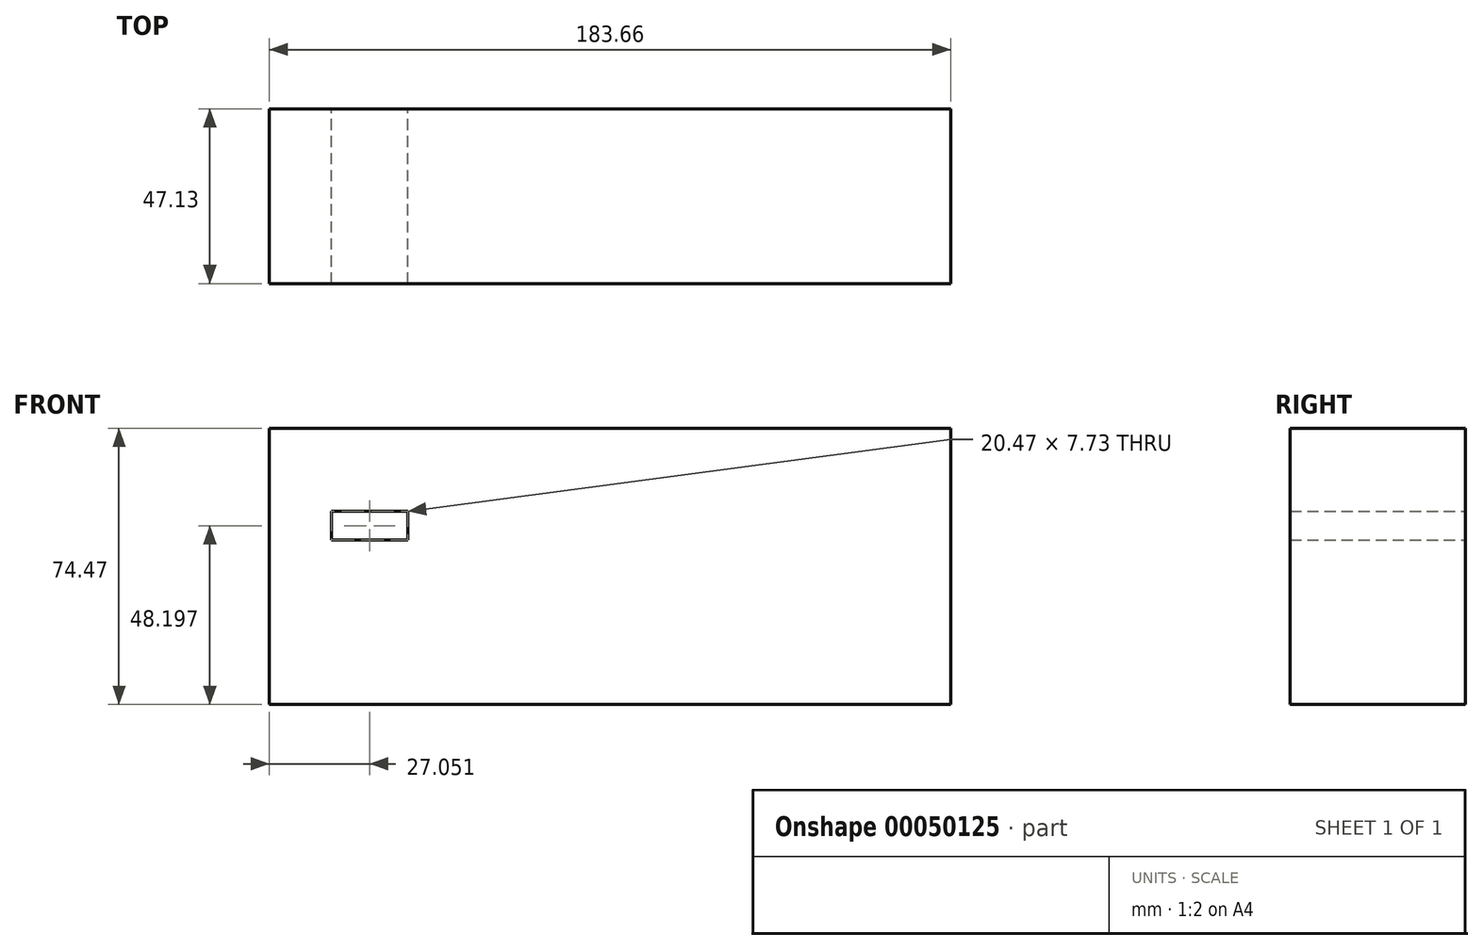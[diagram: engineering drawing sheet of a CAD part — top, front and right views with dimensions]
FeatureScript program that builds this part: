
annotation { "Feature Type Name" : "Feature", "Feature Type Description" : "" }
export const myFeature = defineFeature(function(context is Context, id is Id, definition is map)
    precondition{}
    {
        {
            var Q0;
            Q0=qCreatedBy(makeId("Front.planeOp"),FACE);
            var sketch = newSketch(context, id + "F0", { "sketchPlane" : qUnion([Q0])});
            skLineSegment(sketch, "E0.bottom", {"start": v(-110.36, -2.83) * mm, "end": v(73.3, -2.83) * mm});
            skLineSegment(sketch, "E0.top", {"start": v(-110.36, 71.64) * mm, "end": v(73.3, 71.64) * mm});
            skLineSegment(sketch, "E0.left", {"start": v(-110.36, -2.83) * mm, "end": v(-110.36, 71.64) * mm});
            skLineSegment(sketch, "E0.right", {"start": v(73.3, -2.83) * mm, "end": v(73.3, 71.64) * mm});
            skLineSegment(sketch, "E1.bottom", {"start": v(-93.54, 41.5) * mm, "end": v(-73.08, 41.5) * mm});
            skLineSegment(sketch, "E1.top", {"start": v(-93.54, 49.23) * mm, "end": v(-73.08, 49.23) * mm});
            skLineSegment(sketch, "E1.left", {"start": v(-93.54, 41.5) * mm, "end": v(-93.54, 49.23) * mm});
            skLineSegment(sketch, "E1.right", {"start": v(-73.08, 41.5) * mm, "end": v(-73.08, 49.23) * mm});
            skSolve(sketch);
        }
        {
            var Q0;
            Q0=makeQuery(id+"F0.imprint","IMPRINT",FACE,{"disambiguationData":[TD([[makeQuery(id+"F0.imprint","IMPRINT",EDGE,{"derivedFrom":sQuery(id+"F0.wireOp",EDGE,"E0.bottom")}),1.0]])]});
            extrude(context, id + "F1", {"entities" : qUnion([Q0]), "depth" : 47.13 * mm});
        }
    });
